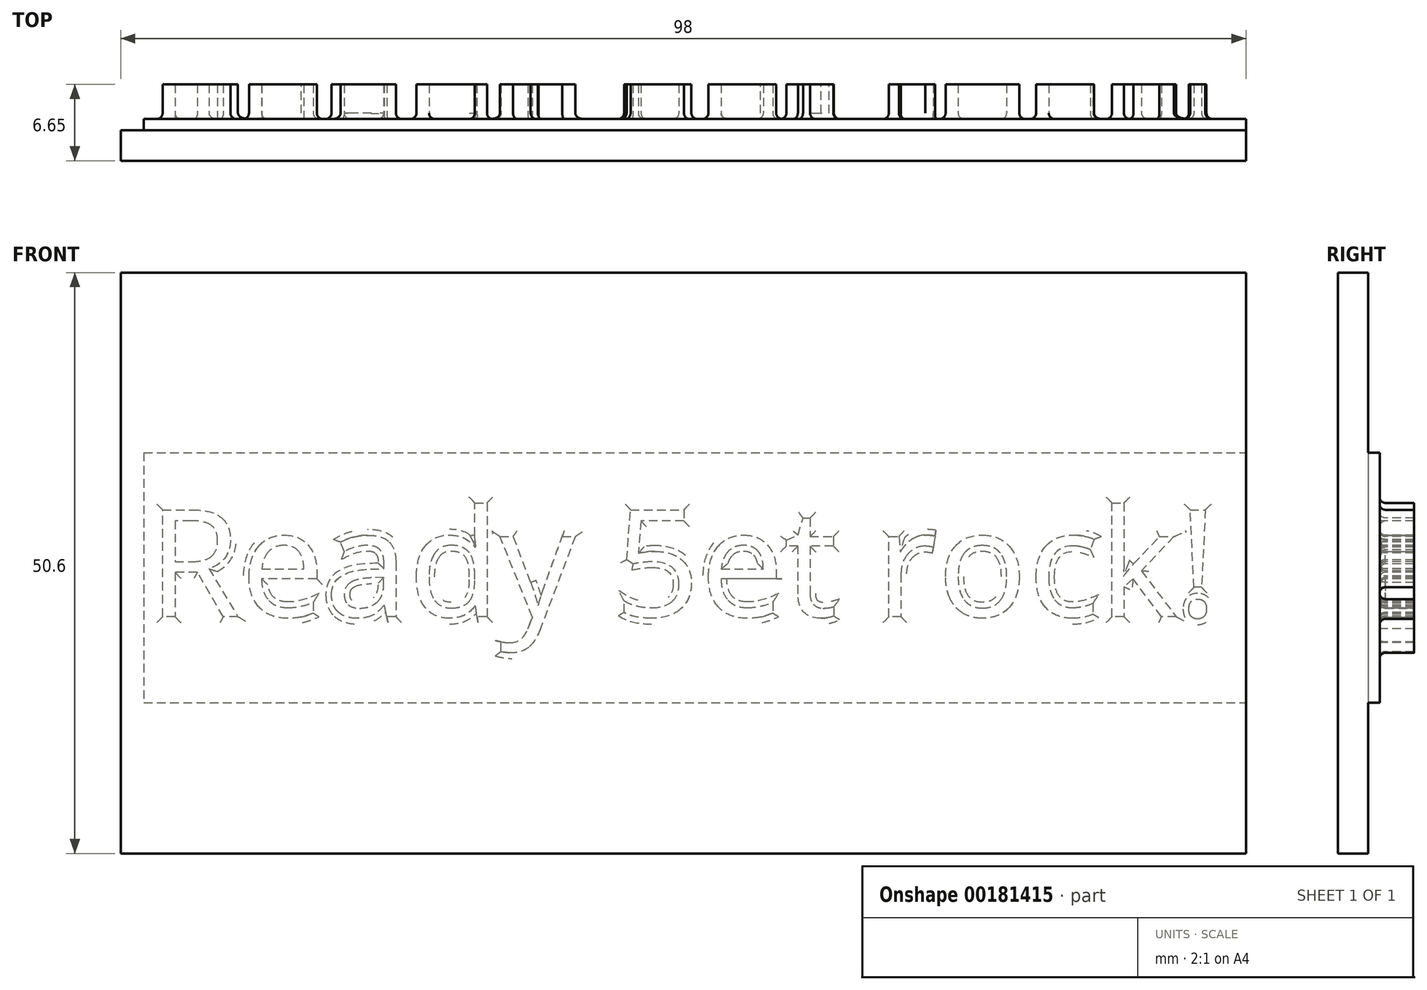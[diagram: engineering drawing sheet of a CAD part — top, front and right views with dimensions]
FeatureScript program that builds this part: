
annotation { "Feature Type Name" : "Feature", "Feature Type Description" : "" }
export const myFeature = defineFeature(function(context is Context, id is Id, definition is map)
    precondition{}
    {
        {
            var Q0;
            Q0=qCreatedBy(makeId("Front.planeOp"),FACE);
            var sketch = newSketch(context, id + "F0", { "sketchPlane" : qUnion([Q0])});
            skLineSegment(sketch, "E0.bottom", {"start": v(-93.36, 14.62) * mm, "end": v(2.64, 14.62) * mm});
            skLineSegment(sketch, "E0.top", {"start": v(-93.36, -7.17) * mm, "end": v(2.64, -7.17) * mm});
            skLineSegment(sketch, "E0.left", {"start": v(-93.36, 14.62) * mm, "end": v(-93.36, -7.17) * mm});
            skLineSegment(sketch, "E0.right", {"start": v(2.64, 14.62) * mm, "end": v(2.64, -7.17) * mm});
            skSolve(sketch);
        }
        {
            var Q0;
            Q0 = qSketchRegion(id + "F0", true);
            extrude(context, id + "F1", {"entities" : qUnion([Q0]), "depth" : 1 * mm});
        }
        {
            var Q0;
            Q0=qCreatedBy(makeId("Front.planeOp"),FACE);
            var sketch = newSketch(context, id + "F2", { "sketchPlane" : qUnion([Q0])});
            skText(sketch, "E1", { "text": "Ready 5et rock!", "fontName": "OpenSans-Regular.ttf"});
            const initialGuessF2  = {"E1": [-0.093, 0.00032, 1, 0, 0.0094]};
            skSetInitialGuess(sketch, initialGuessF2);
            skSolve(sketch);
        }
        {
            var Q0;
            Q0 = qSketchRegion(id + "F2", true);
            extrude(context, id + "F3", {"entities" : qUnion([Q0]), "operationType" : NewBodyOperationType.ADD, "oppositeDirection" : true, "depth" : 3 * mm});
        }
        {
            var Q0;
            Q0=makeQuery(id+"F3.opExtrude","CAP_EDGE",EDGE,{"disambiguationData":[OSD([sQuery(id+"F2.wireOp",EDGE,"E1.sketch_text.stroke-224")])],"isStart":true});
            var Q1;
            Q1=makeQuery(id+"F3.opExtrude","CAP_EDGE",EDGE,{"disambiguationData":[OSD([sQuery(id+"F2.wireOp",EDGE,"E1.sketch_text.stroke-209")])],"isStart":true});
            var Q2;
            Q2=makeQuery(id+"F3.opExtrude","CAP_EDGE",EDGE,{"disambiguationData":[OSD([sQuery(id+"F2.wireOp",EDGE,"E1.sketch_text.stroke-214")])],"isStart":true});
            var Q3;
            Q3=makeQuery(id+"F3.opExtrude","CAP_EDGE",EDGE,{"disambiguationData":[OSD([sQuery(id+"F2.wireOp",EDGE,"E1.sketch_text.stroke-210")])],"isStart":true});
            var Q4;
            Q4=makeQuery(id+"F3.opExtrude","CAP_EDGE",EDGE,{"disambiguationData":[OSD([sQuery(id+"F2.wireOp",EDGE,"E1.sketch_text.stroke-222")])],"isStart":true});
            var Q5;
            Q5=makeQuery(id+"F3.opExtrude","CAP_EDGE",EDGE,{"disambiguationData":[OSD([sQuery(id+"F2.wireOp",EDGE,"E1.sketch_text.stroke-223")])],"isStart":true});
            var Q6;
            Q6=makeQuery(id+"F3.opExtrude","CAP_EDGE",EDGE,{"disambiguationData":[OSD([sQuery(id+"F2.wireOp",EDGE,"E1.sketch_text.stroke-208")])],"isStart":true});
            var Q7;
            Q7=makeQuery(id+"F3.opExtrude","CAP_EDGE",EDGE,{"disambiguationData":[OSD([sQuery(id+"F2.wireOp",EDGE,"E1.sketch_text.stroke-207")])],"isStart":true});
            var Q8;
            Q8=makeQuery(id+"F3.opExtrude","CAP_EDGE",EDGE,{"disambiguationData":[OSD([sQuery(id+"F2.wireOp",EDGE,"E1.sketch_text.stroke-218")])],"isStart":true});
            var Q9;
            Q9=makeQuery(id+"F3.opExtrude","CAP_EDGE",EDGE,{"disambiguationData":[OSD([sQuery(id+"F2.wireOp",EDGE,"E1.sketch_text.stroke-217")])],"isStart":true});
            var Q10;
            Q10=makeQuery(id+"F3.opExtrude","CAP_EDGE",EDGE,{"disambiguationData":[OSD([sQuery(id+"F2.wireOp",EDGE,"E1.sketch_text.stroke-196")])],"isStart":true});
            var Q11;
            Q11=makeQuery(id+"F3.opExtrude","CAP_EDGE",EDGE,{"disambiguationData":[OSD([sQuery(id+"F2.wireOp",EDGE,"E1.sketch_text.stroke-195")])],"isStart":true});
            var Q12;
            Q12=makeQuery(id+"F3.opExtrude","CAP_EDGE",EDGE,{"disambiguationData":[OSD([sQuery(id+"F2.wireOp",EDGE,"E1.sketch_text.stroke-182")])],"isStart":true});
            var Q13;
            Q13=makeQuery(id+"F3.opExtrude","CAP_EDGE",EDGE,{"disambiguationData":[OSD([sQuery(id+"F2.wireOp",EDGE,"E1.sketch_text.stroke-183")])],"isStart":true});
            var Q14;
            Q14=makeQuery(id+"F3.opExtrude","CAP_EDGE",EDGE,{"disambiguationData":[OSD([sQuery(id+"F2.wireOp",EDGE,"E1.sketch_text.stroke-202")])],"isStart":true});
            var Q15;
            Q15=makeQuery(id+"F3.opExtrude","CAP_EDGE",EDGE,{"disambiguationData":[OSD([sQuery(id+"F2.wireOp",EDGE,"E1.sketch_text.stroke-166")])],"isStart":true});
            var Q16;
            Q16=makeQuery(id+"F3.opExtrude","SWEPT_EDGE",EDGE,{"disambiguationData":[OSD([sQuery(id+"F2.wireOp",EDGE,"E1.sketch_text.stroke-158"),sQuery(id+"F2.wireOp",EDGE,"E1.sketch_text.stroke-159")])]});
            var Q17;
            Q17=makeQuery(id+"F3.opExtrude","CAP_EDGE",EDGE,{"disambiguationData":[OSD([sQuery(id+"F2.wireOp",EDGE,"E1.sketch_text.stroke-158")])],"isStart":true});
            var Q18;
            Q18=makeQuery(id+"F3.opExtrude","CAP_EDGE",EDGE,{"disambiguationData":[OSD([sQuery(id+"F2.wireOp",EDGE,"E1.sketch_text.stroke-159")])],"isStart":true});
            var Q19;
            Q19=makeQuery(id+"F3.opExtrude","CAP_EDGE",EDGE,{"disambiguationData":[OSD([sQuery(id+"F2.wireOp",EDGE,"E1.sketch_text.stroke-132")])],"isStart":true});
            var Q20;
            Q20=makeQuery(id+"F3.opExtrude","CAP_EDGE",EDGE,{"disambiguationData":[OSD([sQuery(id+"F2.wireOp",EDGE,"E1.sketch_text.stroke-139")])],"isStart":true});
            var Q21;
            Q21=makeQuery(id+"F3.opExtrude","CAP_EDGE",EDGE,{"disambiguationData":[OSD([sQuery(id+"F2.wireOp",EDGE,"E1.sketch_text.stroke-104")])],"isStart":true});
            var Q22;
            Q22=makeQuery(id+"F3.opExtrude","CAP_EDGE",EDGE,{"disambiguationData":[OSD([sQuery(id+"F2.wireOp",EDGE,"E1.sketch_text.stroke-118")])],"isStart":true});
            var Q23;
            Q23=makeQuery(id+"F3.opExtrude","CAP_EDGE",EDGE,{"disambiguationData":[OSD([sQuery(id+"F2.wireOp",EDGE,"E1.sketch_text.stroke-117")])],"isStart":true});
            var Q24;
            Q24=makeQuery(id+"F3.opExtrude","CAP_EDGE",EDGE,{"disambiguationData":[OSD([sQuery(id+"F2.wireOp",EDGE,"E1.sketch_text.stroke-113")])],"isStart":true});
            var Q25;
            Q25=makeQuery(id+"F3.opExtrude","CAP_EDGE",EDGE,{"disambiguationData":[OSD([sQuery(id+"F2.wireOp",EDGE,"E1.sketch_text.stroke-125")])],"isStart":true});
            var Q26;
            Q26=makeQuery(id+"F3.opExtrude","CAP_EDGE",EDGE,{"disambiguationData":[OSD([sQuery(id+"F2.wireOp",EDGE,"E1.sketch_text.stroke-148")])],"isStart":true});
            var Q27;
            Q27=makeQuery(id+"F3.opExtrude","CAP_EDGE",EDGE,{"disambiguationData":[OSD([sQuery(id+"F2.wireOp",EDGE,"E1.sketch_text.stroke-152")])],"isStart":true});
            var Q28;
            Q28=makeQuery(id+"F3.opExtrude","CAP_EDGE",EDGE,{"disambiguationData":[OSD([sQuery(id+"F2.wireOp",EDGE,"E1.sketch_text.stroke-168")])],"isStart":true});
            var Q29;
            Q29=makeQuery(id+"F3.opExtrude","CAP_EDGE",EDGE,{"disambiguationData":[OSD([sQuery(id+"F2.wireOp",EDGE,"E1.sketch_text.stroke-167")])],"isStart":true});
            var Q30;
            Q30=makeQuery(id+"F3.opExtrude","CAP_EDGE",EDGE,{"disambiguationData":[OSD([sQuery(id+"F2.wireOp",EDGE,"E1.sketch_text.stroke-144")])],"isStart":true});
            var Q31;
            Q31=makeQuery(id+"F3.opExtrude","CAP_EDGE",EDGE,{"disambiguationData":[OSD([sQuery(id+"F2.wireOp",EDGE,"E1.sketch_text.stroke-156")])],"isStart":true});
            var Q32;
            Q32=makeQuery(id+"F3.opExtrude","CAP_EDGE",EDGE,{"disambiguationData":[OSD([sQuery(id+"F2.wireOp",EDGE,"E1.sketch_text.stroke-157")])],"isStart":true});
            var Q33;
            Q33=makeQuery(id+"F3.opExtrude","CAP_EDGE",EDGE,{"disambiguationData":[OSD([sQuery(id+"F2.wireOp",EDGE,"E1.sketch_text.stroke-231")])],"isStart":true});
            var Q34;
            Q34=makeQuery(id+"F3.opExtrude","CAP_EDGE",EDGE,{"disambiguationData":[OSD([sQuery(id+"F2.wireOp",EDGE,"E1.sketch_text.stroke-211")])],"isStart":true});
            var Q35;
            Q35=makeQuery(id+"F3.opExtrude","CAP_EDGE",EDGE,{"disambiguationData":[OSD([sQuery(id+"F2.wireOp",EDGE,"E1.sketch_text.stroke-213")])],"isStart":true});
            var Q36;
            Q36=makeQuery(id+"F3.opExtrude","CAP_EDGE",EDGE,{"disambiguationData":[OSD([sQuery(id+"F2.wireOp",EDGE,"E1.sketch_text.stroke-212")])],"isStart":true});
            var Q37;
            Q37=makeQuery(id+"F3.opExtrude","CAP_EDGE",EDGE,{"disambiguationData":[OSD([sQuery(id+"F2.wireOp",EDGE,"E1.sketch_text.stroke-216")])],"isStart":true});
            var Q38;
            Q38=makeQuery(id+"F3.opExtrude","CAP_EDGE",EDGE,{"disambiguationData":[OSD([sQuery(id+"F2.wireOp",EDGE,"E1.sketch_text.stroke-204")])],"isStart":true});
            var Q39;
            Q39=makeQuery(id+"F3.opExtrude","CAP_EDGE",EDGE,{"disambiguationData":[OSD([sQuery(id+"F2.wireOp",EDGE,"E1.sketch_text.stroke-197")])],"isStart":true});
            var Q40;
            Q40=makeQuery(id+"F3.opExtrude","CAP_EDGE",EDGE,{"disambiguationData":[OSD([sQuery(id+"F2.wireOp",EDGE,"E1.sketch_text.stroke-221")])],"isStart":true});
            var Q41;
            Q41=makeQuery(id+"F3.opExtrude","CAP_EDGE",EDGE,{"disambiguationData":[OSD([sQuery(id+"F2.wireOp",EDGE,"E1.sketch_text.stroke-95")])],"isStart":true});
            var Q42;
            Q42=makeQuery(id+"F3.opExtrude","CAP_EDGE",EDGE,{"disambiguationData":[OSD([sQuery(id+"F2.wireOp",EDGE,"E1.sketch_text.stroke-76")])],"isStart":true});
            var Q43;
            Q43=makeQuery(id+"F3.opExtrude","CAP_EDGE",EDGE,{"disambiguationData":[OSD([sQuery(id+"F2.wireOp",EDGE,"E1.sketch_text.stroke-65")])],"isStart":true});
            var Q44;
            Q44=makeQuery(id+"F3.opExtrude","CAP_EDGE",EDGE,{"disambiguationData":[OSD([sQuery(id+"F2.wireOp",EDGE,"E1.sketch_text.stroke-54")])],"isStart":true});
            var Q45;
            Q45=makeQuery(id+"F3.opExtrude","CAP_EDGE",EDGE,{"disambiguationData":[OSD([sQuery(id+"F2.wireOp",EDGE,"E1.sketch_text.stroke-41")])],"isStart":true});
            var Q46;
            Q46=makeQuery(id+"F3.opExtrude","CAP_EDGE",EDGE,{"disambiguationData":[OSD([sQuery(id+"F2.wireOp",EDGE,"E1.sketch_text.stroke-31")])],"isStart":true});
            var Q47;
            Q47=makeQuery(id+"F3.opExtrude","CAP_EDGE",EDGE,{"disambiguationData":[OSD([sQuery(id+"F2.wireOp",EDGE,"E1.sketch_text.stroke-6")])],"isStart":true});
            var Q48;
            Q48=makeQuery(id+"F3.opExtrude","CAP_EDGE",EDGE,{"disambiguationData":[OSD([sQuery(id+"F2.wireOp",EDGE,"E1.sketch_text.stroke-0")])],"isStart":true});
            var Q49;
            Q49=makeQuery(id+"F3.opExtrude","CAP_EDGE",EDGE,{"disambiguationData":[OSD([sQuery(id+"F2.wireOp",EDGE,"E1.sketch_text.stroke-10")])],"isStart":true});
            var Q50;
            Q50=makeQuery(id+"F3.opExtrude","CAP_EDGE",EDGE,{"disambiguationData":[OSD([sQuery(id+"F2.wireOp",EDGE,"E1.sketch_text.stroke-7")])],"isStart":true});
            var Q51;
            Q51=makeQuery(id+"F3.opExtrude","CAP_EDGE",EDGE,{"disambiguationData":[OSD([sQuery(id+"F2.wireOp",EDGE,"E1.sketch_text.stroke-8")])],"isStart":true});
            var Q52;
            Q52=makeQuery(id+"F3.opExtrude","CAP_EDGE",EDGE,{"disambiguationData":[OSD([sQuery(id+"F2.wireOp",EDGE,"E1.sketch_text.stroke-1")])],"isStart":true});
            var Q53;
            Q53=makeQuery(id+"F3.opExtrude","CAP_EDGE",EDGE,{"disambiguationData":[OSD([sQuery(id+"F2.wireOp",EDGE,"E1.sketch_text.stroke-29")])],"isStart":true});
            var Q54;
            Q54=makeQuery(id+"F3.opExtrude","CAP_EDGE",EDGE,{"disambiguationData":[OSD([sQuery(id+"F2.wireOp",EDGE,"E1.sketch_text.stroke-25")])],"isStart":true});
            var Q55;
            Q55=makeQuery(id+"F3.opExtrude","CAP_EDGE",EDGE,{"disambiguationData":[OSD([sQuery(id+"F2.wireOp",EDGE,"E1.sketch_text.stroke-26")])],"isStart":true});
            var Q56;
            Q56=makeQuery(id+"F3.opExtrude","CAP_EDGE",EDGE,{"disambiguationData":[OSD([sQuery(id+"F2.wireOp",EDGE,"E1.sketch_text.stroke-61")])],"isStart":true});
            var Q57;
            Q57=makeQuery(id+"F3.opExtrude","CAP_EDGE",EDGE,{"disambiguationData":[OSD([sQuery(id+"F2.wireOp",EDGE,"E1.sketch_text.stroke-48")])],"isStart":true});
            var Q58;
            Q58=makeQuery(id+"F3.opExtrude","CAP_EDGE",EDGE,{"disambiguationData":[OSD([sQuery(id+"F2.wireOp",EDGE,"E1.sketch_text.stroke-85")])],"isStart":true});
            var Q59;
            Q59=makeQuery(id+"F3.opExtrude","CAP_EDGE",EDGE,{"disambiguationData":[OSD([sQuery(id+"F2.wireOp",EDGE,"E1.sketch_text.stroke-89")])],"isStart":true});
            var Q60;
            Q60=makeQuery(id+"F3.opExtrude","CAP_EDGE",EDGE,{"disambiguationData":[OSD([sQuery(id+"F2.wireOp",EDGE,"E1.sketch_text.stroke-121")])],"isStart":true});
            var Q61;
            Q61=makeQuery(id+"F3.opExtrude","CAP_EDGE",EDGE,{"disambiguationData":[OSD([sQuery(id+"F2.wireOp",EDGE,"E1.sketch_text.stroke-120")])],"isStart":true});
            var Q62;
            Q62=makeQuery(id+"F3.opExtrude","CAP_EDGE",EDGE,{"disambiguationData":[OSD([sQuery(id+"F2.wireOp",EDGE,"E1.sketch_text.stroke-137")])],"isStart":true});
            var Q63;
            Q63=makeQuery(id+"F3.opExtrude","CAP_EDGE",EDGE,{"disambiguationData":[OSD([sQuery(id+"F2.wireOp",EDGE,"E1.sketch_text.stroke-74")])],"isStart":true});
            var Q64;
            Q64=makeQuery(id+"F3.opExtrude","CAP_EDGE",EDGE,{"disambiguationData":[OSD([sQuery(id+"F2.wireOp",EDGE,"E1.sketch_text.stroke-75")])],"isStart":true});
            var Q65;
            Q65=makeQuery(id+"F3.opExtrude","CAP_EDGE",EDGE,{"disambiguationData":[OSD([sQuery(id+"F2.wireOp",EDGE,"E1.sketch_text.stroke-2")])],"isStart":true});
            var Q66;
            Q66=makeQuery(id+"F3.opExtrude","CAP_EDGE",EDGE,{"disambiguationData":[OSD([sQuery(id+"F2.wireOp",EDGE,"E1.sketch_text.stroke-49")])],"isStart":true});
            var Q67;
            Q67=makeQuery(id+"F3.opExtrude","CAP_EDGE",EDGE,{"disambiguationData":[OSD([sQuery(id+"F2.wireOp",EDGE,"E1.sketch_text.stroke-9")])],"isStart":true});
            var Q68;
            Q68=makeQuery(id+"F3.opExtrude","CAP_EDGE",EDGE,{"disambiguationData":[OSD([sQuery(id+"F2.wireOp",EDGE,"E1.sketch_text.stroke-77")])],"isStart":true});
            var Q69;
            Q69=makeQuery(id+"F3.opExtrude","CAP_EDGE",EDGE,{"disambiguationData":[OSD([sQuery(id+"F2.wireOp",EDGE,"E1.sketch_text.stroke-99")])],"isStart":true});
            var Q70;
            Q70=makeQuery(id+"F3.opExtrude","CAP_EDGE",EDGE,{"disambiguationData":[OSD([sQuery(id+"F2.wireOp",EDGE,"E1.sketch_text.stroke-103")])],"isStart":true});
            var Q71;
            Q71=makeQuery(id+"F3.opExtrude","CAP_EDGE",EDGE,{"disambiguationData":[OSD([sQuery(id+"F2.wireOp",EDGE,"E1.sketch_text.stroke-94")])],"isStart":true});
            var Q72;
            Q72=makeQuery(id+"F3.opExtrude","CAP_EDGE",EDGE,{"disambiguationData":[OSD([sQuery(id+"F2.wireOp",EDGE,"E1.sketch_text.stroke-88")])],"isStart":true});
            var Q73;
            Q73=makeQuery(id+"F3.opExtrude","CAP_EDGE",EDGE,{"disambiguationData":[OSD([sQuery(id+"F2.wireOp",EDGE,"E1.sketch_text.stroke-119")])],"isStart":true});
            var Q74;
            Q74=makeQuery(id+"F3.opExtrude","CAP_EDGE",EDGE,{"disambiguationData":[OSD([sQuery(id+"F2.wireOp",EDGE,"E1.sketch_text.stroke-173")])],"isStart":true});
            var Q75;
            Q75=makeQuery(id+"F3.opExtrude","CAP_EDGE",EDGE,{"disambiguationData":[OSD([sQuery(id+"F2.wireOp",EDGE,"E1.sketch_text.stroke-169")])],"isStart":true});
            var Q76;
            Q76=makeQuery(id+"F3.opExtrude","CAP_EDGE",EDGE,{"disambiguationData":[OSD([sQuery(id+"F2.wireOp",EDGE,"E1.sketch_text.stroke-170")])],"isStart":true});
            var Q77;
            Q77=makeQuery(id+"F3.opExtrude","CAP_EDGE",EDGE,{"disambiguationData":[OSD([sQuery(id+"F2.wireOp",EDGE,"E1.sketch_text.stroke-155")])],"isStart":true});
            var Q78;
            Q78=makeQuery(id+"F3.opExtrude","CAP_EDGE",EDGE,{"disambiguationData":[OSD([sQuery(id+"F2.wireOp",EDGE,"E1.sketch_text.stroke-154")])],"isStart":true});
            var Q79;
            Q79=makeQuery(id+"F3.opExtrude","CAP_EDGE",EDGE,{"disambiguationData":[OSD([sQuery(id+"F2.wireOp",EDGE,"E1.sketch_text.stroke-153")])],"isStart":true});
            var Q80;
            Q80=makeQuery(id+"F3.opExtrude","CAP_EDGE",EDGE,{"disambiguationData":[OSD([sQuery(id+"F2.wireOp",EDGE,"E1.sketch_text.stroke-151")])],"isStart":true});
            var Q81;
            Q81=makeQuery(id+"F3.opExtrude","CAP_EDGE",EDGE,{"disambiguationData":[OSD([sQuery(id+"F2.wireOp",EDGE,"E1.sketch_text.stroke-150")])],"isStart":true});
            var Q82;
            Q82=makeQuery(id+"F3.opExtrude","CAP_EDGE",EDGE,{"disambiguationData":[OSD([sQuery(id+"F2.wireOp",EDGE,"E1.sketch_text.stroke-149")])],"isStart":true});
            var Q83;
            Q83=makeQuery(id+"F3.opExtrude","CAP_EDGE",EDGE,{"disambiguationData":[OSD([sQuery(id+"F2.wireOp",EDGE,"E1.sketch_text.stroke-116")])],"isStart":true});
            var Q84;
            Q84=makeQuery(id+"F3.opExtrude","CAP_EDGE",EDGE,{"disambiguationData":[OSD([sQuery(id+"F2.wireOp",EDGE,"E1.sketch_text.stroke-109")])],"isStart":true});
            var Q85;
            Q85=makeQuery(id+"F3.opExtrude","CAP_EDGE",EDGE,{"disambiguationData":[OSD([sQuery(id+"F2.wireOp",EDGE,"E1.sketch_text.stroke-134")])],"isStart":true});
            var Q86;
            Q86=makeQuery(id+"F3.opExtrude","CAP_EDGE",EDGE,{"disambiguationData":[OSD([sQuery(id+"F2.wireOp",EDGE,"E1.sketch_text.stroke-215")])],"isStart":true});
            var Q87;
            Q87=makeQuery(id+"F3.opExtrude","CAP_EDGE",EDGE,{"disambiguationData":[OSD([sQuery(id+"F2.wireOp",EDGE,"E1.sketch_text.stroke-55")])],"isStart":true});
            fillet(context, id + "F4", {"entities" : qUnion([Q0, Q1, Q2, Q3, Q4, Q5, Q6, Q7, Q8, Q9, Q10, Q11, Q12, Q13, Q14, Q15, Q16, Q17, Q18, Q19, Q20, Q21, Q22, Q23, Q24, Q25, Q26, Q27, Q28, Q29, Q30, Q31, Q32, Q33, Q34, Q35, Q36, Q37, Q38, Q39, Q40, Q41, Q42, Q43, Q44, Q45, Q46, Q47, Q48, Q49, Q50, Q51, Q52, Q53, Q54, Q55, Q56, Q57, Q58, Q59, Q60, Q61, Q62, Q63, Q64, Q65, Q66, Q67, Q68, Q69, Q70, Q71, Q72, Q73, Q74, Q75, Q76, Q77, Q78, Q79, Q80, Q81, Q82, Q83, Q84, Q85, Q86, Q87]), "radius" : 0.5 * mm, "tangentPropagation" : true, "allowEdgeOverflow" : false});
        }
        {
            var Q0;
            Q0=makeQuery(id+"F1.opExtrude","SWEPT_FACE",FACE,{"disambiguationData":[OSD([sQuery(id+"F0.wireOp",EDGE,"E0.right")])]});
            var sketch = newSketch(context, id + "F5", { "sketchPlane" : qUnion([Q0])});
            skLineSegment(sketch, "E2.bottom", {"start": v(-1, -20.3) * mm, "end": v(-3.65, -20.3) * mm});
            skLineSegment(sketch, "E2.top", {"start": v(-1, 30.3) * mm, "end": v(-3.65, 30.3) * mm});
            skLineSegment(sketch, "E2.left", {"start": v(-1, -20.3) * mm, "end": v(-1, 30.3) * mm});
            skLineSegment(sketch, "E2.right", {"start": v(-3.65, -20.3) * mm, "end": v(-3.65, 30.3) * mm});
            skLineSegment(sketch, "E3", {"start": v(-3.65, 5) * mm, "end": v(-1, 5) * mm, "construction": true});
            skSolve(sketch);
        }
        {
            var Q0;
            {var subQ5=sQuery(id+"F5.wireOp",EDGE,"E2.bottom");Q0=makeQuery(id+"F5.imprint","IMPRINT",FACE,{"disambiguationData":[TD([[makeQuery(id+"F5.imprint","IMPRINT",EDGE,{"derivedFrom":subQ5}),-1.0]])]});}
            extrude(context, id + "F6", {"entities" : qUnion([Q0]), "operationType" : NewBodyOperationType.ADD, "oppositeDirection" : true, "depth" : 98 * mm});
        }
    });
